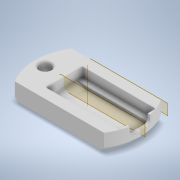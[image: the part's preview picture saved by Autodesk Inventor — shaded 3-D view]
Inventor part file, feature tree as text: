
AUTODESK INVENTOR PART (.ipt)
format: ipt  version: 2021 (Build 250183000, 183)  size: 620,544 bytes
history: native  units: in
note: dims shown in document units (in); Inventor stores cm internally (conversion verified against a paired STEP export)
features: extrude x8, sketch x8, fillet x3, chamfer x2, plane x2, other x1, pattern_circular x1, mirror x1
ambient origin geometry x8: Origin, YZ Plane, XZ Plane, XY Plane, X Axis, Y Axis, Z Axis, Center Point
bodies: Solid1 (feature_tree)
feature tree (26):
  extrude  "Extrusion1"  Depth=0.315in TaperAngle=0.0deg
  chamfer  "Chamfer2"  Distance=0.189in
  extrude  "Extrusion2"  Depth=0.1575in
  extrude  "Extrusion3"  Depth=0.2205in
  other  "Work Axis1"
  plane  "Work Plane1"
  extrude  "Extrusion5"  Depth=0.0315in
  extrude  "Extrusion4"  Depth=0.0315in
  fillet  "Fillet4"  Radius=0.5in
  pattern_circular  "Circular Pattern2"  [2 undecoded]
  chamfer  "Chamfer3"  Distance=0.25in
  fillet  "Fillet7"  [1 undecoded]
  extrude  "Extrusion9"  Depth=0.0315in TaperAngle=0.0deg
  extrude  "Extrusion10"  Depth=0.0315in
  fillet  "Fillet9"  Radius=0.0394in
  plane  "Work Plane3"
  extrude  "Extrusion11"  TaperAngle=45.0deg  [1 undecoded]
  mirror  "Mirror5"
  sketch  "Sketch1"  dims[d0=2.0472in d3=0.315in d4=0.0in]
  sketch  "Sketch2"  dims[d5=1.4236in]
  sketch  "Sketch3"  dims[d6=0.7079in]
  sketch  "Sketch4"  dims[d7=0.3539in]
  sketch  "Sketch7"  dims[d8=0.4646in d9=0.189in d10=0.0in]
  sketch  "Sketch12"  dims[d11=0.0in d14=0.1575in]
  sketch  "Sketch13"  dims[d15=0.0in d16=0.0in d17=0.2205in]
  sketch  "Sketch15"  dims[d18=0.2047in d19=0.0in d23=0.8268in d24=0.3539in d28=0.5in d29=1.4in d30=0.25in d31=0.0in d32=0.063in d33=0.0in d44=0.1575in d47=0.0394in d48=0.0in d49=0.0in d51=0.0in d54=0.063in d55=0.0in d56=45.0deg d58=0.0394in d59=0.1181in d60=1.9685in d61=240.0deg d63=0.0591in d64=0.1969in d65=45.0deg d72=0.0315in d79=0.1039in d80=0.9517in d81=0.4759in d82=0.9728in d83=0.4864in d84=0.0394in d85=0.0in d86=0.547in d87=0.2735in d88=0.0787in d89=0.0in d90=0.0787in d92=-0.1969in d93=0.5906in d94=0.0in d91=0.0197in]
note: 4 required parameter values undecoded (feature->parameter linkage not recoverable at this tier; creation-order binding heuristic only, values carry confidence <= 0.55)
